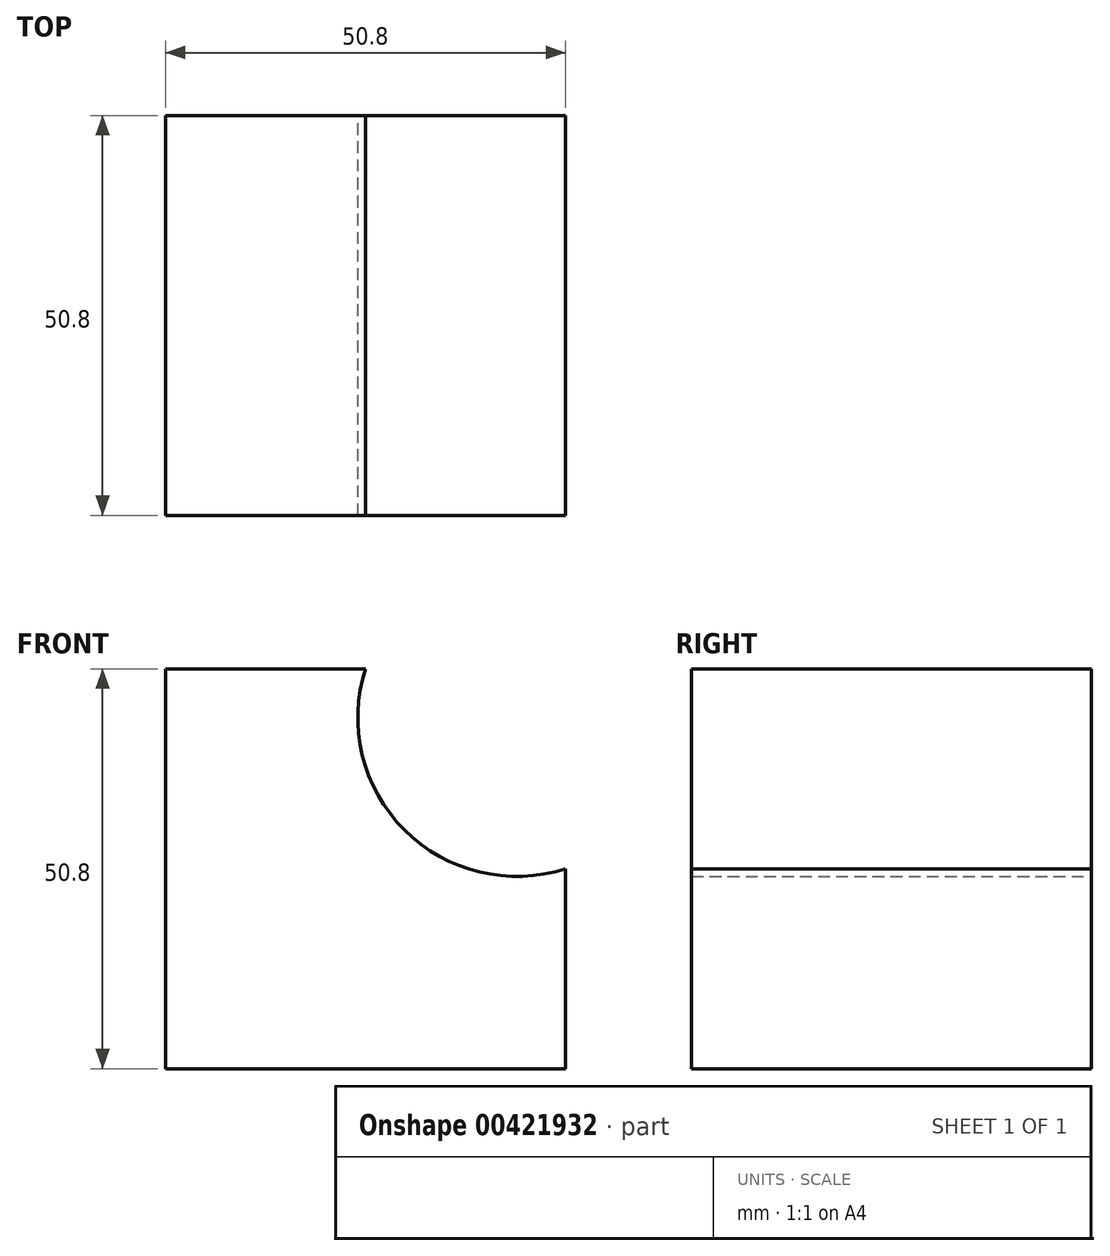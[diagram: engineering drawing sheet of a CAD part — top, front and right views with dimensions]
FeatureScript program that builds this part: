
annotation { "Feature Type Name" : "Feature", "Feature Type Description" : "" }
export const myFeature = defineFeature(function(context is Context, id is Id, definition is map)
    precondition{}
    {
        {
            var Q0;
            Q0=qCreatedBy(makeId("Front.planeOp"),FACE);
            var sketch = newSketch(context, id + "F0", { "sketchPlane" : qUnion([Q0])});
            skLineSegment(sketch, "E0", {"start": v(0, 0) * mm, "end": v(-50.8, 0) * mm});
            skLineSegment(sketch, "E1", {"start": v(-50.8, 0) * mm, "end": v(-50.8, 50.8) * mm});
            skLineSegment(sketch, "E2", {"start": v(-50.8, 50.8) * mm, "end": v(-25.4, 50.8) * mm});
            skLineSegment(sketch, "E3", {"start": v(0, 25.4) * mm, "end": v(0, 0) * mm});
            skArc(sketch, "E4", {"start": v(-25.4, 50.8) * mm, "mid": v(-20.47, 30.33) * mm, "end": v(0, 25.4) * mm});
            skSolve(sketch);
        }
        {
            var Q0;
            Q0=makeQuery(id+"F0.imprint","IMPRINT",FACE,{"disambiguationData":[TD([[makeQuery(id+"F0.imprint","IMPRINT",EDGE,{"derivedFrom":sQuery(id+"F0.wireOp",EDGE,"E0")}),-1.0]])]});
            extrude(context, id + "F1", {"entities" : qUnion([Q0]), "depth" : 50.8 * mm});
        }
    });
